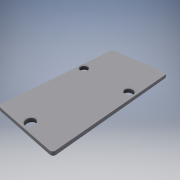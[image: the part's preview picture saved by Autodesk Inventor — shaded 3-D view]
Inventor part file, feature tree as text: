
AUTODESK INVENTOR PART (.ipt)
format: ipt  version: 2019.4 (Build 234330000, 330)  size: 114,688 bytes
history: native  units: mm
features: extrude x1, sketch x1
ambient origin geometry x8: Origin, YZ Plane, XZ Plane, XY Plane, X Axis, Y Axis, Z Axis, Center Point
bodies: Solide1 (feature_tree)
feature tree (2):
  extrude  "Extrusion1"  Depth=25.0mm
  sketch  "Esquisse1"
